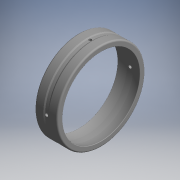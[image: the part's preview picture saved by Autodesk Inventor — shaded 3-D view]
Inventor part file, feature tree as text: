
AUTODESK INVENTOR PART (.ipt)
format: ipt  version: 2017.3 (Build 213256000, 256)  size: 196,096 bytes
history: native  units: mm (DEFAULTED — no unit token found)
features: other x14, revolve x4, sketch x4
ambient origin geometry x8: Origin, YZ Plane, XZ Plane, XY Plane, X Axis, Y Axis, Z Axis, Center Point
bodies: Solid1 (feature_tree)
feature tree (22):
  revolve  "Revolution1"  Angle=360.0deg
  revolve  "Revolution2"  Angle=360.0deg
  revolve  "Revolution3"  [1 undecoded]
  revolve  "Revolution4"  [1 undecoded]
  other  "NO_GEO_XY"
  other  "NO_GEO_YZ"
  other  "NO_GEO_ZX"
  other  "NO_GEO_X"
  other  "NO_GEO_Y"
  other  "NO_GEO_Z"
  other  "NO_GEO_Center"
  other  "or_XY"
  other  "or_YZ"
  other  "or_ZX"
  other  "or_X"
  other  "or_Y"
  other  "or_Z"
  other  "or_Center"
  sketch  "Sketch_5"  dims[d2=360.0deg d3=360.0deg]
  sketch  "Sketch_2"  dims[d0=360.0deg d1=360.0deg]
  sketch  "Sketch_9"  dims[d4=0.0mm]
  sketch  "Sketch_10"
note: 2 required parameter values undecoded (feature->parameter linkage not recoverable at this tier; creation-order binding heuristic only, values carry confidence <= 0.55)
